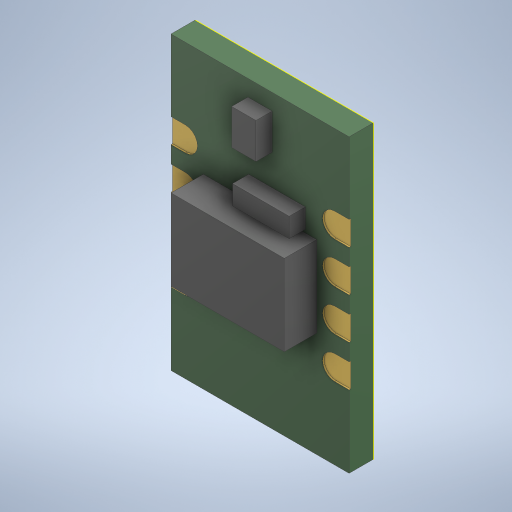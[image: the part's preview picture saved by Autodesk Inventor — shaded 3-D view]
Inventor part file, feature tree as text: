
AUTODESK INVENTOR PART (.ipt)
format: ipt  version: 2024.1 (Build 281209000, 209)  size: 1,397,760 bytes
history: native  units: mm
features: extrude x7, sketch x6, projected_geometry x2, other x1, imported_body x1
ambient origin geometry x8: Origin, YZ Plane, XZ Plane, XY Plane, X Axis, Y Axis, Z Axis, Center Point
bodies: Body1 (feature_tree)
feature tree (17):
  other  "ソリッド1"
  extrude  "押し出し1"  Depth=1.5mm TaperAngle=0.0deg
  extrude  "押し出し2"  Depth=11.0mm
  sketch  "スケッチ3"
  extrude  "押し出し3"  Depth=18.0mm
  extrude  "押し出し4"  Depth=1.5mm TaperAngle=0.0deg
  extrude  "押し出し5"  Depth=2.0mm
  extrude  "押し出し6"  Depth=5.0mm
  sketch  "スケッチ6"
  extrude  "押し出し7"  Depth=1.5mm
  sketch  "スケッチ1"
  sketch  "スケッチ2"
  sketch  "スケッチ4"
  sketch  "スケッチ5"
  projected_geometry  "投影ループ1"
  projected_geometry  "投影ループ2"
  imported_body  "Base1"
